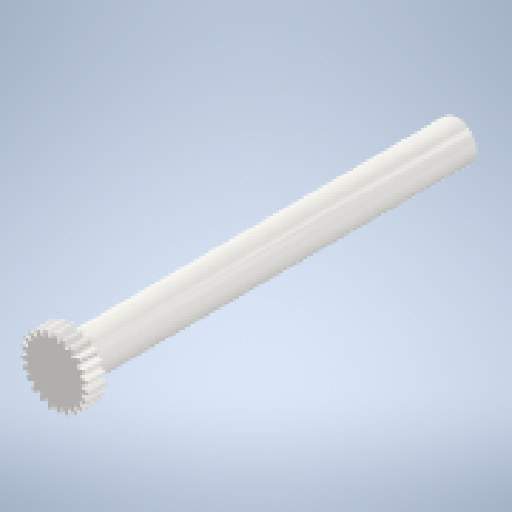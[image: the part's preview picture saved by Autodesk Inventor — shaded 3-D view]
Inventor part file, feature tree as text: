
AUTODESK INVENTOR PART (.ipt)
format: ipt  version: 2023.2 (Build 272271000, 271)  size: 271,872 bytes
history: native  units: mm (DEFAULTED — no unit token found)
features: plane x3, other x3, sketch x3, extrude x2
ambient origin geometry x8: Origin, YZ Plane, XZ Plane, XY Plane, X Axis, Y Axis, Z Axis, Center Point
bodies: Solid1 (feature_tree)
feature tree (11):
  extrude  "Extrusion1"  Depth=5.0mm TaperAngle=0.0deg
  plane  "Work Plane2"
  plane  "Work Plane8"
  plane  "Work Plane9"
  other  "Spur Gear"
  extrude  "Extrusion2"  Depth=10.0mm TaperAngle=0.0deg
  sketch  "Sketch1"  dims[d0=17.506247mm d1=5.0mm d2=0.0mm]
  sketch  "Sketch2"  dims[d3=16.1mm d4=10.0mm d5=0.0mm]
  other  "Srf1"
  sketch  "Sketch3"  dims[d16=12.604893mm d17=0.0mm d34=1.36591mm d39=0.0mm d41=0.0mm d43=12.604893mm d46=12.604893mm d47=0.0mm d48=0.0mm d49=10.0mm d50=100.0mm d51=0.0mm]
  other  "Pitch Diameter"
